# Revit family: PRESTO ALPA 90 ARTE-E con valvula de vaciado
name_source: partatom
category: Aparatos sanitarios
revit_build: Autodesk Revit 2015 (Build: 20140223_1515(x64)
units: mm (PartAtom-declared; Revit-internal decimal feet)

## types (1)
- 98941
    Accionamiento = Por pulsador
    CAUDAL = 8 L/Min
    CIERRE = Automático en 30 seg.
    Comentarios de tipo = ◦Componentes fabricados en materiales que soportan temperaturas de hasta 70º C, para permitir la realización de desinfecciones térmicas anti-legionella
◦Cabeza intercambiable que comprende todo el sistema de temporización
◦Apertura por pulsador de mando único con selección de temperatura mediante giro de 180º
◦Válvulas antirretorno incorporadas conformes a la norma EN 1717, que impiden la intercomunicación del agua fría con la caliente
◦Posibilidad de posicionar el mando de Regulación con un tope de temperatura
◦Suministrado con filtros
◦Tapa en acero inoxidable de 200 x 200 mm
◦Caja de empotrar y placa de fijación intermedia fabricadas con protección antioxidante.
    Conexión AC = Sí
    Conexión AF = Sí
    Código de montaje = C1030220
    Descripción = Grifo temporizado mezclador para instalación empotrada con cuerpo de latón y pulsador ARTE cromado. Regulador automático de caudal.
    ENTRADA = Macho y hembra 3/4"
    Elevación por defecto = 1219 mm
    Fabricante = PRESTO IBÉRICA
    Imagen de tipo = <Ninguno>
    Material = Presto Ibérica: LATON CROMADO
    Modelo = ALPA 90 ARTE E
    PESO BRUTO = 2.580  Kg
    REFERENCIA = 98941
    TIPO DE AGUA = Fria/Caliente
    Teléfono = (+34) 915 782 575
    URL = http://www.prestoiberica.com
